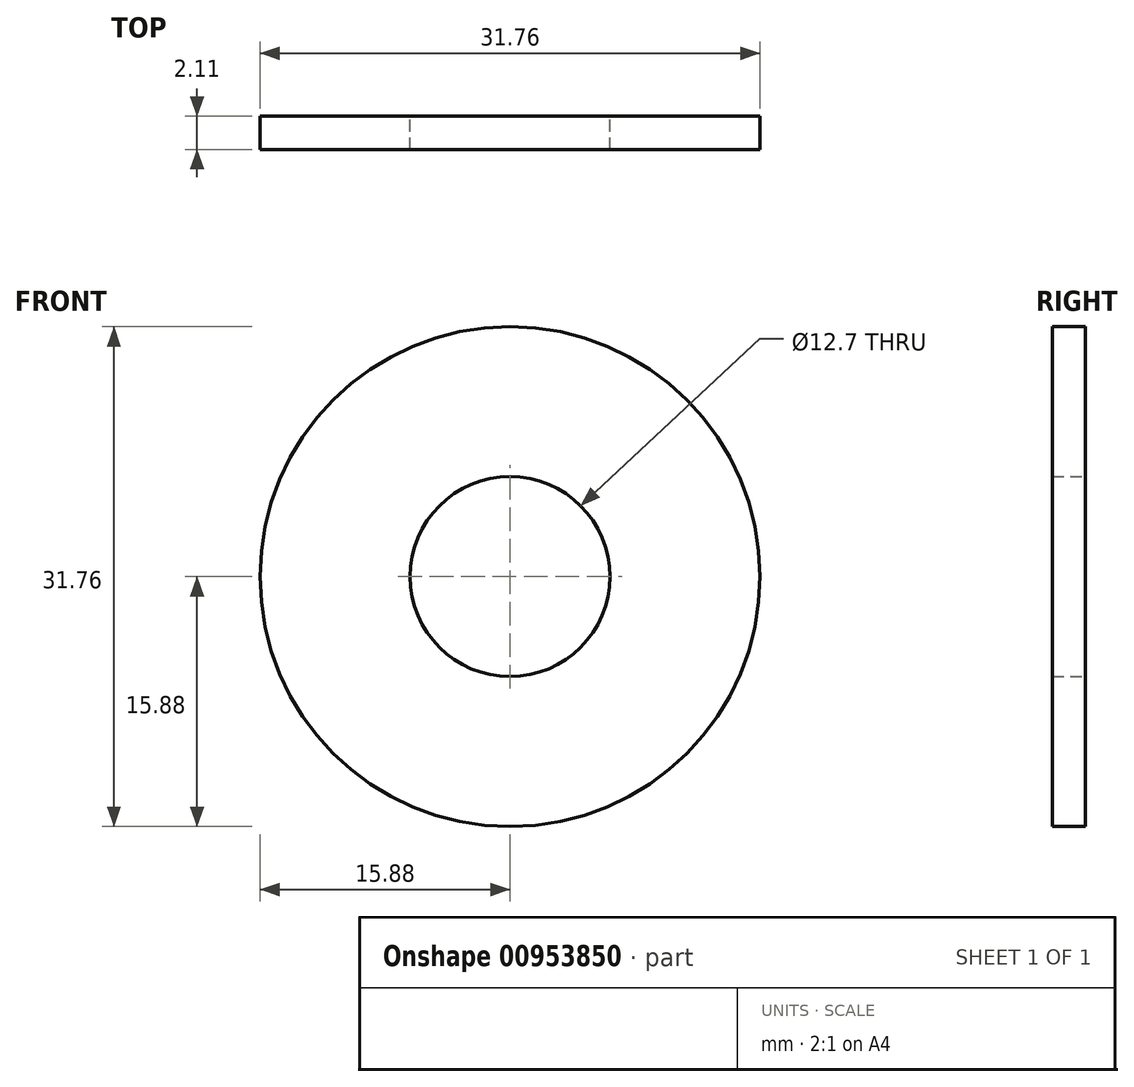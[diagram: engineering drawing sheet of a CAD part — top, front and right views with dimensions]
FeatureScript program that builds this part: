
annotation { "Feature Type Name" : "Feature", "Feature Type Description" : "" }
export const myFeature = defineFeature(function(context is Context, id is Id, definition is map)
    precondition{}
    {
        {
            var Q0;
            Q0=qCreatedBy(makeId("Front.planeOp"),FACE);
            var sketch = newSketch(context, id + "F0", { "sketchPlane" : qUnion([Q0])});
            skCircle(sketch, "E0", {"center": v(0, 0) * mm, "radius": 15.88 * mm});
            skCircle(sketch, "E1", {"center": v(0, 0) * mm, "radius": 6.35 * mm});
            skSolve(sketch);
        }
        {
            var Q0;
            Q0 = qSketchRegion(id + "F0", true);
            extrude(context, id + "F1", {"entities" : qUnion([Q0]), "depth" : 2.1 * mm, "offsetDistance" : 25.4 * mm});
        }
    });
